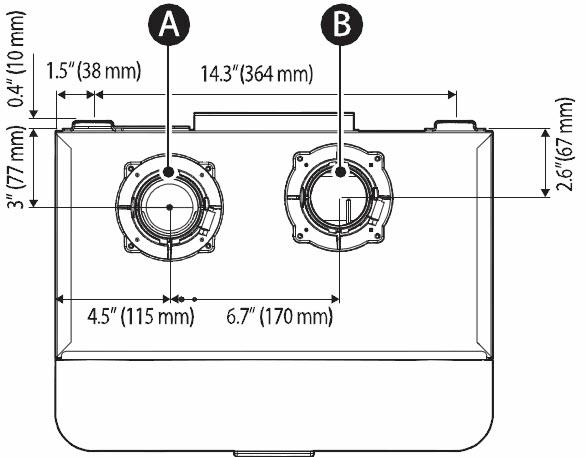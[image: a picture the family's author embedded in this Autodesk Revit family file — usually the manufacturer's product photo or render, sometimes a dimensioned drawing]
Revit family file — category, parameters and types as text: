
# Revit family: Water_Heater-Racks-Navien-NPE-6_Unit_Front-03
name_source: partatom
category: Mechanical Equipment
revit_build: Autodesk Revit 2016 (Build: 20150220_1215(x64)
units: mm (PartAtom-declared; Revit-internal decimal feet)

## family parameters
Cut with Voids When Loaded = No
Host = Face
OmniClass Number = 23.65.35.11
OmniClass Title = Supply Water Heaters
Part Type = Normal
Room Calculation Point = No
Round Connector Dimension = Use Diameter
Shared = No

## types (4) — shared parameters
2" Exhaust/Intake = Yes
3" Exhaust/Intake = No
Apparent Load = 0 VA
Assembly Code = D3010500
Certifications = Energy Star | AHRI | CSA | CSA | NFS
Cold Water Inlet = 1"
Configuration = NPE_F6_4F2F
Default Elevation = 48 "
Depth = 23.8 "
Description = 6 Unit Front
Exhaust = 2"
Finish = Metal - Navien - White
Flow Rate = 1 GPM
Flow Rate Note = 35°F (19°C) temp rise: 11.2 GPM (42 L/m) | 45°F (25°C) temp rise: 8.7 GPM (33 L/m) | 67°F (36°C) temp rise: NPE-240A: 5.6 GPM(21 L/m), NPE-240S: 5.7 GPM(22 L/m)
Frequency = 60 Hz
Gas Inlet = 1"
Heating Capacity = 120000.0 Btu/h
Heating Capacity Note = 19,900–199,900 (BTU/H)
Height = 65.5 "
Hot Water Outlet = 1"
Ignition = Electronic ignition
Installation Type = Indoor
Intake = 2"
Keynote = 22 33 00.A1
Manifold(s) = (1) 30019040A + (1) 30019043A
Manufacturer = Navien, Inc.
Manufacturer Fax Number = (949) 420-0430
Natural Gas Manifold Pressure = -0.05" WC to -0.58" WC
Natural Gas Supply Pressure = 3.5"–10.5" WC
Number of Poles = 1
Phase = 1
Power Factor = 1
Product Documentation Link = https://www.navieninc.com
Product Name = NPE Series Tankless Water Heaters w/ Racks
Product Page URL = https://www.navieninc.com
Propane Gas Manifold Pressure = -0.10" WC to -0.78" WC
Propane Gas Supply Pressure = 8"–13" WC
Rack(s) = (1) GFFM-KDIZUS-003 + (5) GFFM-KDIZUS-004
Required Cascade Operation Accessory = (6) 30014367A (Common Vent Damper & Cascade Communication Cable) or (5) GXXX000546 (Individual Vent Cascade Communication Cable)
Type Comments = For Wall Mount RL Manifold systems- Exclude Base & Add-on Racks
URL = https://www.navieninc.com
Venting = Exhaust: 2" PVC, CPVC, PP, SS / 2" special gas vent type BH (Class II, A/B/C) | Intake: 2" PVC, CPVC, PP, SS / 2" special gas vent type BH (Class II, A/B/C) | Vent clearances: 0" to combustibles
Venting Type = Forced draft direct vent
Version = 2016 - v1.0.a
Voltage = 120 V
Water Pressure = 15–150 PSI
Wi-Fi Ready = NaviLink Wi-Fi Control: PBCM-AS-001
Width = 122.3 "

## per-type parameters (varying)
| type | Constraints | Model | Natural Gas | Propane Gas | Recirculation Inlet | Recirculation Inlet Visibility | Tankless Water Heaters | Weight |
| Natural Gas - Recirculating System - NPE-240A(Advanced)-NG | 6 | (6) NPE-240A-NG | Yes | No | 0" | Yes | (6) NPE-240A-NG | 82.00 lbf |
| Natural Gas - NPE-240S(Standard)-NG | 7 | (6) NPE-240S-NG | Yes | No | 1" | No | (6) NPE-240S-NG | 75.00 lbf |
| Propane Gas - Recirculating System - NPE-240A(Advanced)-LPG | 6 | (6) NPE-240A-LPG | No | Yes | 0" | Yes | (6) NPE-240A-LPG | 82.00 lbf |
| Propane Gas - NPE-240S(Standard)-LPG | 7 | (6) NPE-240S-LPG | No | Yes | 1" | No | (6) NPE-240S-LPG | 75.00 lbf |

## geometry (parser evidence)
native form markers: Sweep x20
no freeform markers — native parametric forms only
